# Revit family: C_PPRC_2DO_Cad_MULT_Prod
name_source: partatom
category: Detail Items
revit_build: Autodesk Revit 2014 (Build: 20130308_1515(x64)
units: mm (PartAtom-declared; Revit-internal decimal feet)

## types (2) — shared parameters
Density = 1.50 kg
Description = Post bases
EPD = https://www.strongtie.eu
ETA / DoP = https://www.strongtie.eu
Manufacturer = Simpson Strong-Tie
Model = PPRC
Model Disclaimer = Contact Simpson Strong-Tie Company  for more information
Model ID = 0257257932142463589452113932420325002899
Name = PPRC
ObjectType = PPRC
Product Material = ElectroGalvanised
Product Type = Post bases
Reference = PPRC
Technical datasheet = https://www.strongtie.eu
URL = www.strongtie.eu
UniClass Number = Pr_20_29_31_44
UniClass Title = Joist hangers

## per-type parameters (varying)
| type | _visiblefront | _visibletop |
| SST_PPRC_Front | Yes | No |
| SST_PPRC_Top | No | Yes |

## geometry (parser evidence)
native form markers: Sweep x2
no freeform markers — native parametric forms only
